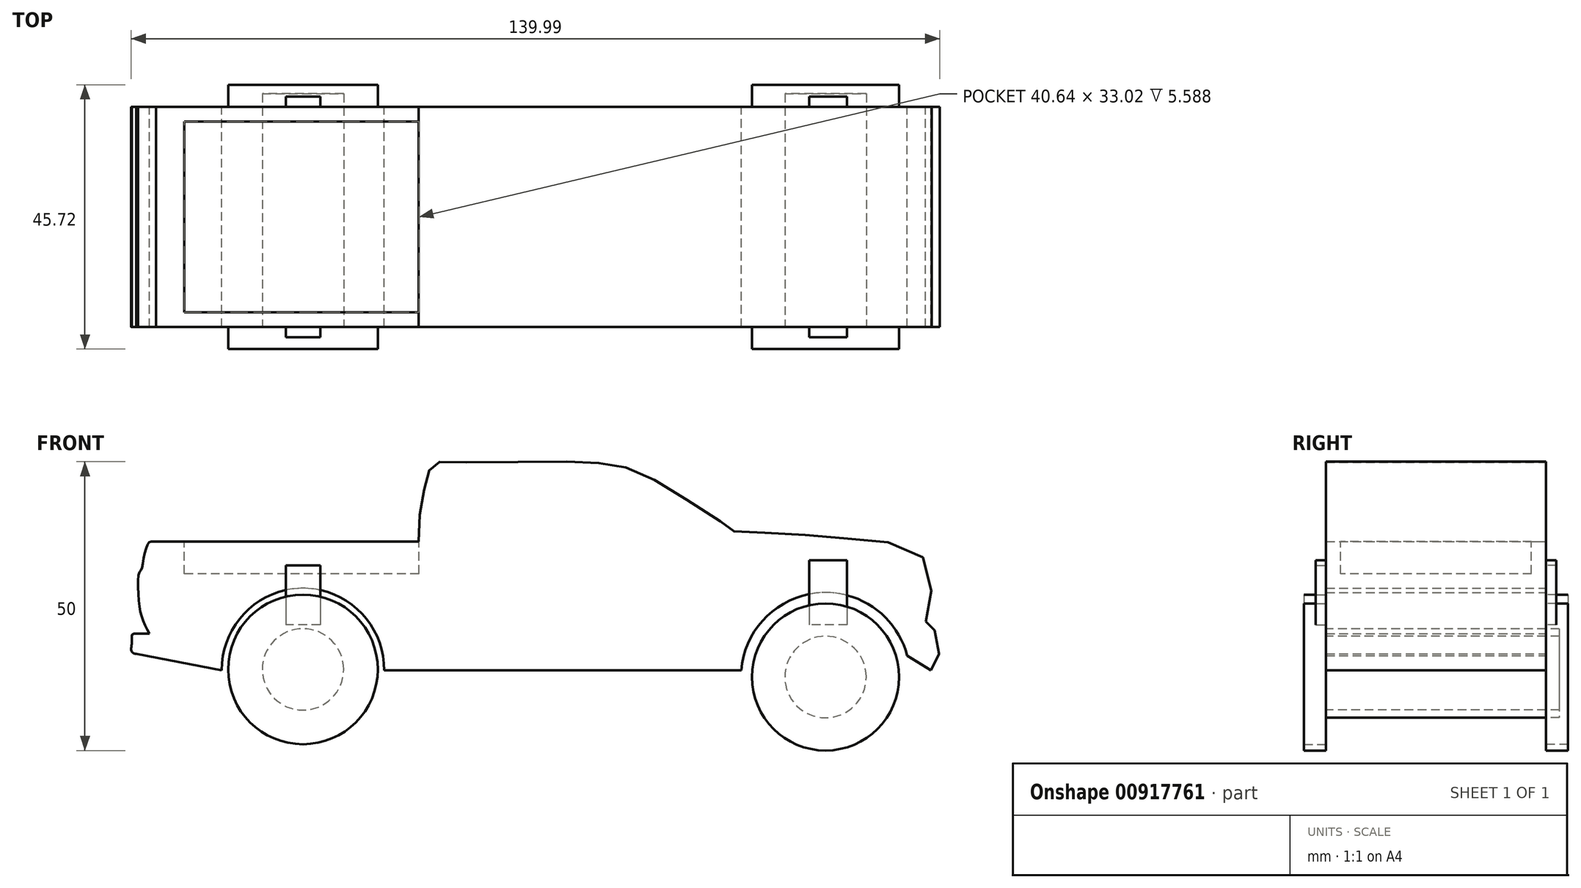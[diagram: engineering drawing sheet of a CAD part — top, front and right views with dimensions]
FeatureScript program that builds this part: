
annotation { "Feature Type Name" : "Feature", "Feature Type Description" : "" }
export const myFeature = defineFeature(function(context is Context, id is Id, definition is map)
    precondition{}
    {
        {
            var Q0;
            Q0=qCreatedBy(makeId("Front.planeOp"),FACE);
            var sketch = newSketch(context, id + "F0", { "sketchPlane" : qUnion([Q0])});
            skLineSegment(sketch, "E0", {"start": v(-69.28, -5.05) * mm, "end": v(-54.44, -7.9) * mm});
            skArc(sketch, "E1", {"start": v(-26.35, -7.9) * mm, "mid": v(-40.4, 6.31) * mm, "end": v(-54.44, -7.9) * mm});
            skLineSegment(sketch, "E2", {"start": v(-26.35, -7.9) * mm, "end": v(35.5, -7.9) * mm});
            skArc(sketch, "E3", {"start": v(64.23, -5.37) * mm, "mid": v(48.8, 5.52) * mm, "end": v(35.5, -7.9) * mm});
            skLineSegment(sketch, "E4", {"start": v(64.23, -5.37) * mm, "end": v(68.33, -7.9) * mm});
            skFitSpline(sketch, "E5", {"points": [v(68.33, -7.9) * mm, v(69.38, -6.41) * mm, v(69.33, -1.25) * mm, v(67.6, -0.59) * mm, v(67.98, 2.63) * mm, v(66.92, 11.71) * mm, v(54.4, 14.88) * mm, v(42.45, 15.83) * mm, v(34.05, 16.2) * mm, v(33.8, 16.47) * mm, v(26.75, 21.16) * mm, v(17.77, 26.41) * mm, v(11.79, 27.91) * mm, v(3.15, 28.23) * mm, v(-15.04, 28.17) * mm, v(-17.24, 28.1) * mm, v(-18.34, 27.09) * mm, v(-19.19, 24.5) * mm, v(-20.06, 19.98) * mm, v(-20.36, 14.4) * mm], "startDerivative": vector(37.65, 32.41) * mm, "endDerivative": vector(-2.3, -108.14) * mm});
            skLineSegment(sketch, "E6", {"start": v(-20.36, 14.4) * mm, "end": v(-65.83, 14.4) * mm});
            skFitSpline(sketch, "E7", {"points": [v(-65.83, 14.4) * mm, v(-66.62, 14.4) * mm, v(-67.11, 14.18) * mm, v(-67.88, 12) * mm, v(-68.38, 9.57) * mm, v(-68.8, 8.91) * mm, v(-68.85, 4.5) * mm, v(-68.2, 1.02) * mm, v(-66.98, -1.56) * mm], "startDerivative": vector(-10.65, 0.35) * mm, "endDerivative": vector(9.08, -16.9) * mm});
            skLineSegment(sketch, "E8", {"start": v(-66.98, -1.56) * mm, "end": v(-69.28, -1.56) * mm});
            skFitSpline(sketch, "E9", {"points": [v(-69.28, -1.56) * mm, v(-69.94, -1.69) * mm, v(-70.04, -3) * mm, v(-70.05, -4.66) * mm, v(-69.28, -5.05) * mm], "startDerivative": vector(-3.85, 0.31) * mm, "endDerivative": vector(4.27, -0.96) * mm});
            skSolve(sketch);
        }
        {
            var Q0;
            Q0 = qSketchRegion(id + "F0", true);
            extrude(context, id + "F1", {"entities" : qUnion([Q0]), "endBound" : BoundingType.SYMMETRIC, "depth" : 38.1 * mm, "offsetDistance" : 25.4 * mm});
        }
        {
            var Q0;
            Q0=makeQuery(id+"F1.opExtrude","SWEPT_FACE",FACE,{"disambiguationData":[OSD([sQuery(id+"F0.wireOp",EDGE,"E6")])]});
            var sketch = newSketch(context, id + "F2", { "sketchPlane" : qUnion([Q0])});
            skLineSegment(sketch, "E10.bottom", {"start": v(-20.33, 16.51) * mm, "end": v(-60.97, 16.51) * mm});
            skLineSegment(sketch, "E10.top", {"start": v(-20.33, -16.5) * mm, "end": v(-60.97, -16.51) * mm});
            skLineSegment(sketch, "E10.left", {"start": v(-20.33, 16.51) * mm, "end": v(-20.33, -16.5) * mm});
            skLineSegment(sketch, "E10.right", {"start": v(-60.97, 16.51) * mm, "end": v(-60.97, -16.51) * mm});
            skSolve(sketch);
        }
        {
            var Q0;
            Q0 = qSketchRegion(id + "F2", true);
            extrude(context, id + "F3", {"entities" : qUnion([Q0]), "operationType" : NewBodyOperationType.REMOVE, "oppositeDirection" : true, "depth" : 5.6 * mm, "offsetDistance" : 25.4 * mm});
        }
        {
            var Q0;
            Q0=makeQuery(id+"F1.opExtrude","CAP_FACE",FACE,{"disambiguationData":[OSD([sQuery(id+"F0.wireOp",EDGE,"E0"),sQuery(id+"F0.wireOp",EDGE,"E1"),sQuery(id+"F0.wireOp",EDGE,"E2"),sQuery(id+"F0.wireOp",EDGE,"E3"),sQuery(id+"F0.wireOp",EDGE,"E4"),sQuery(id+"F0.wireOp",EDGE,"E5"),sQuery(id+"F0.wireOp",EDGE,"E6"),sQuery(id+"F0.wireOp",EDGE,"E7"),sQuery(id+"F0.wireOp",EDGE,"E8"),sQuery(id+"F0.wireOp",EDGE,"E9")])],"isStart":true});
            var sketch = newSketch(context, id + "F4", { "sketchPlane" : qUnion([Q0])});
            skCircle(sketch, "E11", {"center": v(40.4, -7.73) * mm, "radius": 12.95 * mm});
            skCircle(sketch, "E12", {"center": v(-50.08, -9.04) * mm, "radius": 12.73 * mm});
            skSolve(sketch);
        }
        {
            var Q0;
            Q0 = qSketchRegion(id + "F4", true);
            extrude(context, id + "F5", {"entities" : qUnion([Q0]), "depth" : 3.8 * mm, "offsetDistance" : 25.4 * mm});
        }
        {
            var Q0;
            Q0=makeQuery(id+"F5.opExtrude","SWEPT_BODY",BODY,{"disambiguationData":[OSD([sQuery(id+"F4.wireOp",EDGE,"E11")])]});
            var Q1;
            Q1=makeQuery(id+"F5.opExtrude","SWEPT_BODY",BODY,{"disambiguationData":[OSD([sQuery(id+"F4.wireOp",EDGE,"E12")])]});
            var Q2;
            Q2=qCreatedBy(makeId("Front.planeOp"),FACE);
            mirror(context, id + "F6", {"entities" : qUnion([Q0, Q1]), "mirrorPlane" : qUnion([Q2])});
        }
        {
            var Q0;
            Q0=makeQuery(id+"F6.opPattern","COPY",FACE,{"derivedFrom":makeQuery(id+"F5.opExtrude","CAP_FACE",FACE,{"disambiguationData":[OSD([sQuery(id+"F4.wireOp",EDGE,"E11")])],"isStart":true}),"instanceName":"1"});
            var sketch = newSketch(context, id + "F7", { "sketchPlane" : qUnion([Q0])});
            skCircle(sketch, "E13", {"center": v(40.4, -7.73) * mm, "radius": 7.04 * mm});
            skSolve(sketch);
        }
        {
            var Q0;
            Q0=makeQuery(id+"F6.opPattern","COPY",FACE,{"derivedFrom":makeQuery(id+"F5.opExtrude","CAP_FACE",FACE,{"disambiguationData":[OSD([sQuery(id+"F4.wireOp",EDGE,"E12")])],"isStart":true}),"instanceName":"1"});
            var sketch = newSketch(context, id + "F8", { "sketchPlane" : qUnion([Q0])});
            skCircle(sketch, "E14", {"center": v(-50.08, -9.04) * mm, "radius": 7.05 * mm});
            skSolve(sketch);
        }
        {
            var Q0;
            Q0 = qSketchRegion(id + "F7", true);
            var Q1;
            Q1 = qSketchRegion(id + "F8", true);
            extrude(context, id + "F9", {"entities" : qUnion([Q0, Q1]), "depth" : 40.4 * mm, "offsetDistance" : 25.4 * mm});
        }
        {
            var Q0;
            Q0=makeQuery(id+"F1.opExtrude","CAP_FACE",FACE,{"disambiguationData":[OSD([sQuery(id+"F0.wireOp",EDGE,"E0"),sQuery(id+"F0.wireOp",EDGE,"E1"),sQuery(id+"F0.wireOp",EDGE,"E2"),sQuery(id+"F0.wireOp",EDGE,"E3"),sQuery(id+"F0.wireOp",EDGE,"E4"),sQuery(id+"F0.wireOp",EDGE,"E5"),sQuery(id+"F0.wireOp",EDGE,"E6"),sQuery(id+"F0.wireOp",EDGE,"E7"),sQuery(id+"F0.wireOp",EDGE,"E8"),sQuery(id+"F0.wireOp",EDGE,"E9")])],"isStart":true});
            var sketch = newSketch(context, id + "F10", { "sketchPlane" : qUnion([Q0])});
            skPoint(sketch, "E15.firstSnap0", {"position": v(43.1, 14.4) * mm});
            skPoint(sketch, "E15.oppositeSnap0", {"position": v(40.4, 6.31) * mm});
            skLineSegment(sketch, "E16.bottom", {"start": v(37.4, 10.29) * mm, "end": v(43.39, 10.29) * mm});
            skLineSegment(sketch, "E16.top", {"start": v(37.4, 0) * mm, "end": v(43.39, 0) * mm});
            skLineSegment(sketch, "E16.left", {"start": v(37.4, 10.29) * mm, "end": v(37.4, 0) * mm});
            skLineSegment(sketch, "E16.right", {"start": v(43.39, 10.29) * mm, "end": v(43.39, 0) * mm});
            skSolve(sketch);
        }
        {
            var Q0;
            Q0 = qSketchRegion(id + "F10", true);
            var Q1;
            Q1 = qSketchRegion(id + "F12", true);
            extrude(context, id + "F11", {"entities" : qUnion([Q0, Q1]), "depth" : 1.78 * mm, "offsetDistance" : 25.4 * mm});
        }
        {
            var Q0;
            Q0=makeQuery(id+"F1.opExtrude","CAP_FACE",FACE,{"disambiguationData":[OSD([sQuery(id+"F0.wireOp",EDGE,"E0"),sQuery(id+"F0.wireOp",EDGE,"E1"),sQuery(id+"F0.wireOp",EDGE,"E2"),sQuery(id+"F0.wireOp",EDGE,"E3"),sQuery(id+"F0.wireOp",EDGE,"E4"),sQuery(id+"F0.wireOp",EDGE,"E5"),sQuery(id+"F0.wireOp",EDGE,"E6"),sQuery(id+"F0.wireOp",EDGE,"E7"),sQuery(id+"F0.wireOp",EDGE,"E8"),sQuery(id+"F0.wireOp",EDGE,"E9")])],"isStart":true});
            var sketch = newSketch(context, id + "F12", { "sketchPlane" : qUnion([Q0])});
            skLineSegment(sketch, "E17.bottom", {"start": v(-53.81, 11.14) * mm, "end": v(-47.26, 11.14) * mm});
            skLineSegment(sketch, "E17.top", {"start": v(-53.81, 0) * mm, "end": v(-47.26, 0) * mm});
            skLineSegment(sketch, "E17.left", {"start": v(-53.81, 11.14) * mm, "end": v(-53.81, 0) * mm});
            skLineSegment(sketch, "E17.right", {"start": v(-47.26, 11.14) * mm, "end": v(-47.26, 0) * mm});
            skSolve(sketch);
        }
        {
            var Q0;
            Q0 = qSketchRegion(id + "F12", true);
            extrude(context, id + "F13", {"entities" : qUnion([Q0]), "depth" : 1.78 * mm, "offsetDistance" : 25.4 * mm});
        }
        {
            var Q0;
            Q0=makeQuery(id+"F13.opExtrude","SWEPT_BODY",BODY,{"disambiguationData":[OSD([sQuery(id+"F12.wireOp",EDGE,"E17.bottom"),sQuery(id+"F12.wireOp",EDGE,"E17.top"),sQuery(id+"F12.wireOp",EDGE,"E17.left"),sQuery(id+"F12.wireOp",EDGE,"E17.right")])]});
            var Q1;
            Q1=makeQuery(id+"F11.opExtrude","SWEPT_BODY",BODY,{"disambiguationData":[OSD([sQuery(id+"F10.wireOp",EDGE,"E15.bottom"),sQuery(id+"F10.wireOp",EDGE,"E15.top"),sQuery(id+"F10.wireOp",EDGE,"E15.left"),sQuery(id+"F10.wireOp",EDGE,"E15.right")])]});
            var Q2;
            Q2=makeQuery(id+"F11.opExtrude","SWEPT_BODY",BODY,{"disambiguationData":[OSD([sQuery(id+"F10.wireOp",EDGE,"E16.bottom"),sQuery(id+"F10.wireOp",EDGE,"E16.top"),sQuery(id+"F10.wireOp",EDGE,"E16.left"),sQuery(id+"F10.wireOp",EDGE,"E16.right")])]});
            var Q3;
            Q3=qCreatedBy(makeId("Front.planeOp"),FACE);
            mirror(context, id + "F14", {"entities" : qUnion([Q0, Q1, Q2]), "mirrorPlane" : qUnion([Q3])});
        }
    });
